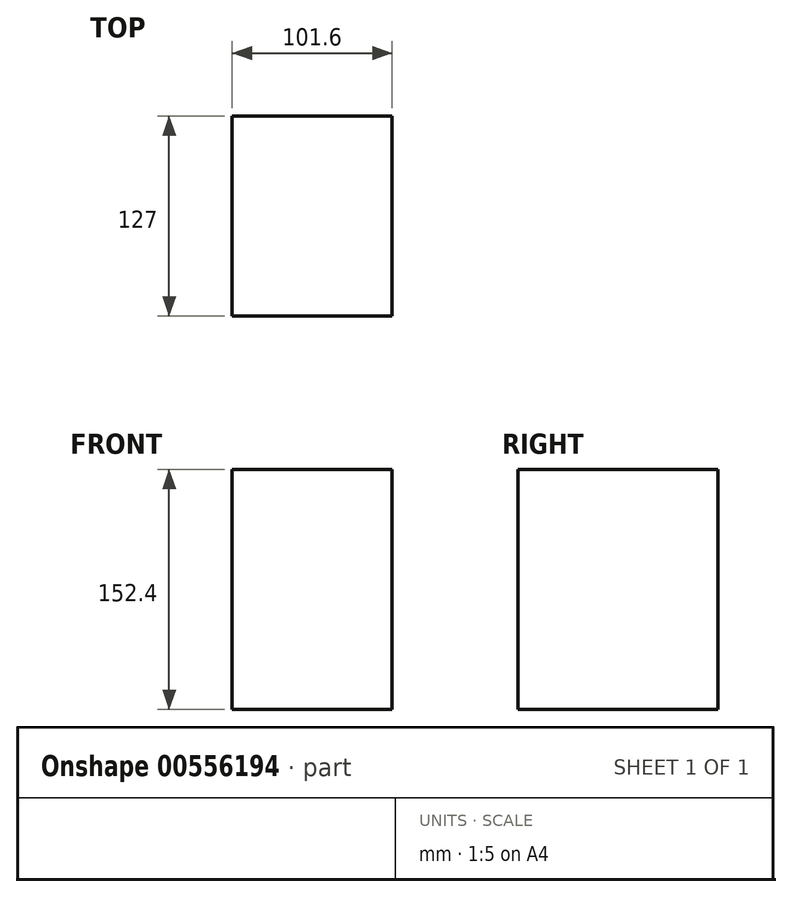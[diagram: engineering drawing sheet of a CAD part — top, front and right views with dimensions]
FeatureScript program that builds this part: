
annotation { "Feature Type Name" : "Feature", "Feature Type Description" : "" }
export const myFeature = defineFeature(function(context is Context, id is Id, definition is map)
    precondition{}
    {
        {
            var Q0;
            Q0=qCreatedBy(makeId("Top.planeOp"),FACE);
            var sketch = newSketch(context, id + "F0", { "sketchPlane" : qUnion([Q0])});
            skLineSegment(sketch, "E0.bottom", {"start": v(-50.8, -63.5) * mm, "end": v(50.8, -63.5) * mm});
            skLineSegment(sketch, "E0.top", {"start": v(-50.8, 63.5) * mm, "end": v(50.8, 63.5) * mm});
            skLineSegment(sketch, "E0.left", {"start": v(-50.8, -63.5) * mm, "end": v(-50.8, 63.5) * mm});
            skLineSegment(sketch, "E0.right", {"start": v(50.8, -63.5) * mm, "end": v(50.8, 63.5) * mm});
            skPoint(sketch, "E0.middle", {"position": v(0, 0) * mm});
            skLineSegment(sketch, "E1", {"start": v(0, 63.5) * mm, "end": v(0, 0) * mm, "construction": true});
            skSolve(sketch);
        }
        {
            var Q0;
            Q0 = qSketchRegion(id + "F0", true);
            extrude(context, id + "F1", {"entities" : qUnion([Q0]), "depth" : 152.4 * mm, "offsetDistance" : 25.4 * mm});
        }
    });
